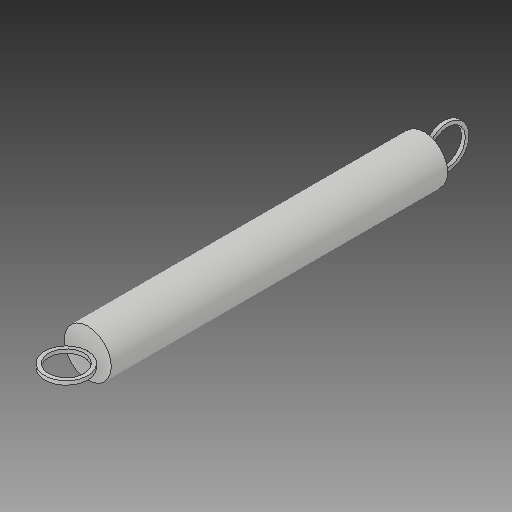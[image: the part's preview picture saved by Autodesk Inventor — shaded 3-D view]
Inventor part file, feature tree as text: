
AUTODESK INVENTOR PART (.ipt)
format: ipt  version: 2018 (Build 220112000, 112)  size: 100,352 bytes
history: native  units: in
note: dims shown in document units (in); Inventor stores cm internally (conversion verified against a paired STEP export)
features: other x3, sketch x3
ambient origin geometry x8: Origin, YZ Plane, XZ Plane, XY Plane, X Axis, Y Axis, Z Axis, Center Point
bodies: Solid1 (feature_tree)
feature tree (6):
  other  "spring stand in.ipt"
  other  "Solid1::spring stand in.ipt"
  other  "TaggingFeature1"
  sketch  "Sketch2"  dims[d0=0.3937in]
  sketch  "Sketch3"
  sketch  "Sketch4"
